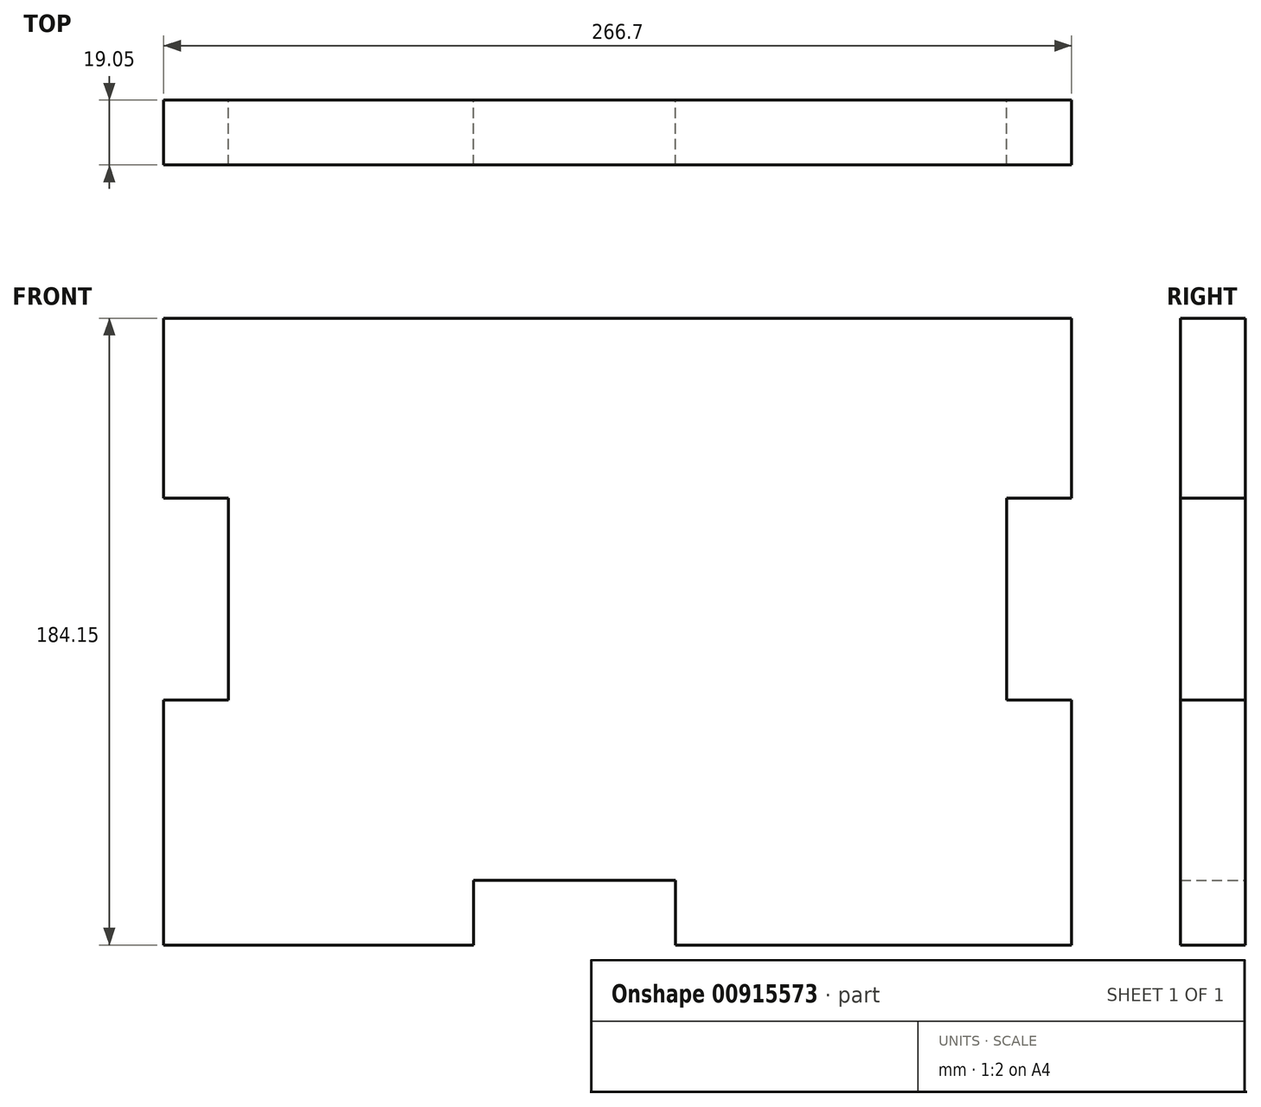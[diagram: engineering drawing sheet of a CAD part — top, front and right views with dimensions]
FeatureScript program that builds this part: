
annotation { "Feature Type Name" : "Feature", "Feature Type Description" : "" }
export const myFeature = defineFeature(function(context is Context, id is Id, definition is map)
    precondition{}
    {
        {
            var Q0;
            Q0=qCreatedBy(makeId("Front.planeOp"),FACE);
            var sketch = newSketch(context, id + "F0", { "sketchPlane" : qUnion([Q0])});
            skPoint(sketch, "E0.middle", {"position": v(0, 0) * mm});
            skLineSegment(sketch, "E1", {"start": v(-133.35, 0) * mm, "end": v(-133.35, 29.63) * mm});
            skLineSegment(sketch, "E2", {"start": v(-133.35, 0) * mm, "end": v(-133.35, -29.63) * mm});
            skLineSegment(sketch, "E3", {"start": v(-133.35, 29.63) * mm, "end": v(-152.4, 29.63) * mm});
            skLineSegment(sketch, "E4", {"start": v(-133.35, -29.63) * mm, "end": v(-152.4, -29.63) * mm});
            skLineSegment(sketch, "E5", {"start": v(-152.4, -29.63) * mm, "end": v(-152.4, -82.55) * mm});
            skLineSegment(sketch, "E6", {"start": v(-61.38, -82.55) * mm, "end": v(-61.38, -101.6) * mm});
            skLineSegment(sketch, "E7", {"start": v(-61.38, -101.6) * mm, "end": v(-152.4, -101.6) * mm});
            skLineSegment(sketch, "E8", {"start": v(-152.4, -101.6) * mm, "end": v(-152.4, -29.63) * mm});
            skLineSegment(sketch, "E9", {"start": v(-61.38, -82.55) * mm, "end": v(-2.12, -82.55) * mm});
            skLineSegment(sketch, "E10", {"start": v(-2.12, -82.55) * mm, "end": v(-2.12, -101.6) * mm});
            skLineSegment(sketch, "E11", {"start": v(-152.4, 29.63) * mm, "end": v(-152.4, 82.55) * mm});
            skLineSegment(sketch, "E12.right", {"start": v(95.25, -29.63) * mm, "end": v(95.25, 29.63) * mm});
            skLineSegment(sketch, "E13.left", {"start": v(114.3, 82.55) * mm, "end": v(114.3, 29.63) * mm});
            skLineSegment(sketch, "E14.right", {"start": v(114.3, -101.6) * mm, "end": v(114.3, -29.63) * mm});
            skLineSegment(sketch, "E15", {"start": v(-2.12, -101.6) * mm, "end": v(114.3, -101.6) * mm});
            skLineSegment(sketch, "E16", {"start": v(95.25, -29.63) * mm, "end": v(114.3, -29.63) * mm});
            skLineSegment(sketch, "E17", {"start": v(95.25, 29.63) * mm, "end": v(114.3, 29.63) * mm});
            skLineSegment(sketch, "E18", {"start": v(114.3, 82.55) * mm, "end": v(-152.4, 82.55) * mm});
            skSolve(sketch);
        }
        {
            var Q0;
            Q0=makeQuery(id+"F0.imprint","IMPRINT",FACE,{"disambiguationData":[TD([[makeQuery(id+"F0.imprint","IMPRINT",EDGE,{"derivedFrom":sQuery(id+"F0.wireOp",EDGE,"E1")}),-1.0]])]});
            extrude(context, id + "F1", {"entities" : qUnion([Q0]), "depth" : 19.05 * mm, "offsetDistance" : 25.4 * mm});
        }
    });
